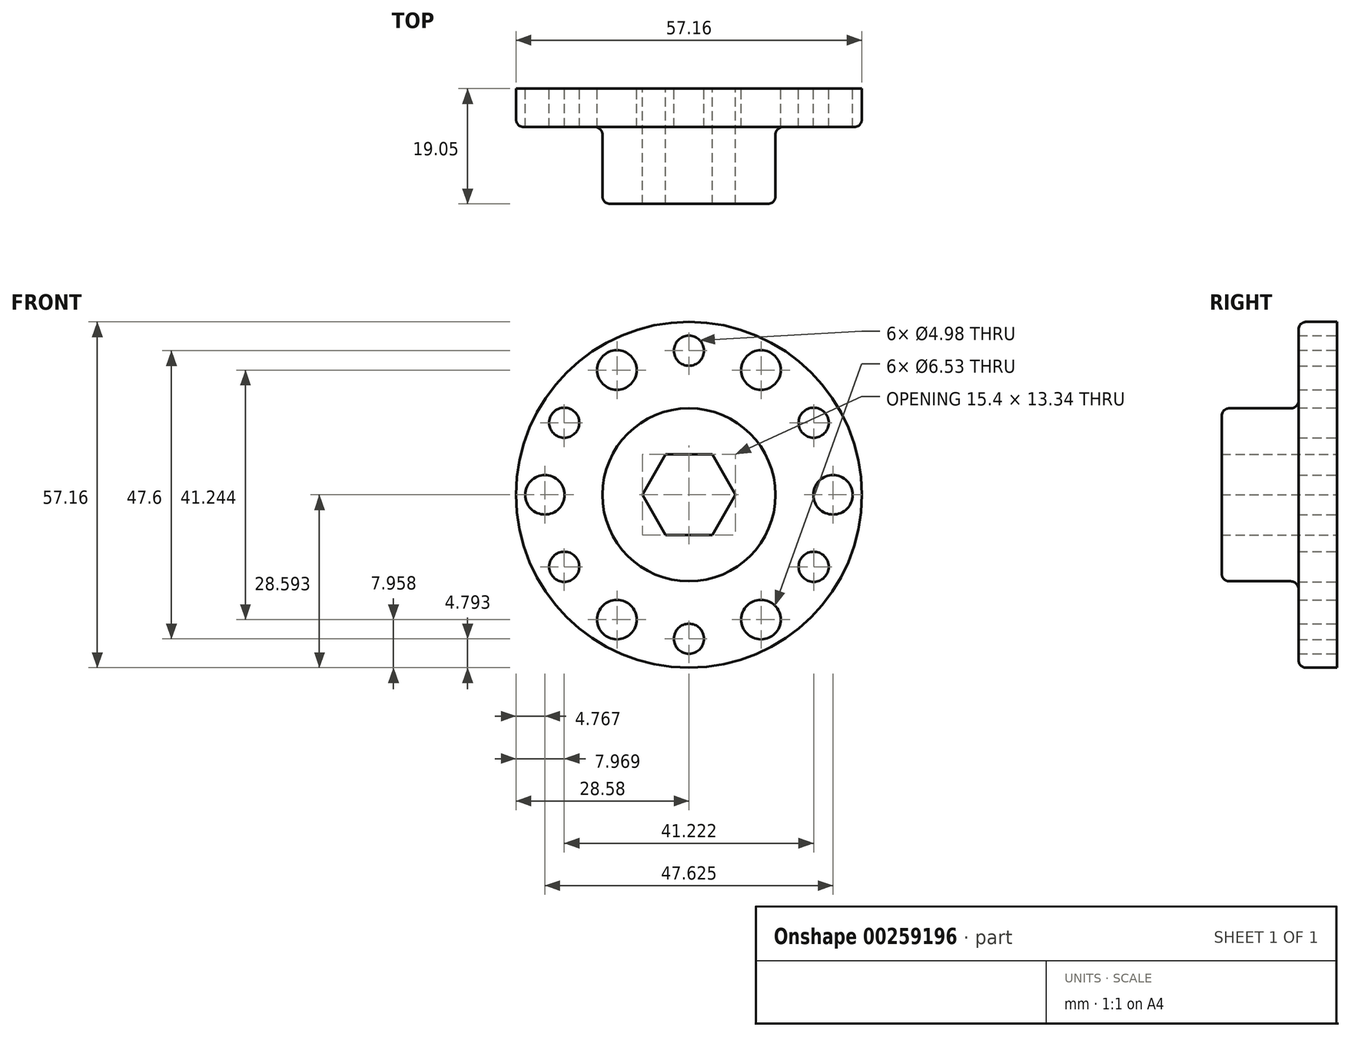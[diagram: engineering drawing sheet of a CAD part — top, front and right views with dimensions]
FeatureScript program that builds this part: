
annotation { "Feature Type Name" : "Feature", "Feature Type Description" : "" }
export const myFeature = defineFeature(function(context is Context, id is Id, definition is map)
    precondition{}
    {
        {
            var Q0;
            Q0=qCreatedBy(makeId("Front.planeOp"),FACE);
            var sketch = newSketch(context, id + "F0", { "sketchPlane" : qUnion([Q0])});
            skCircle(sketch, "E0", {"center": v(0, 0) * mm, "radius": 28.58 * mm});
            skCircle(sketch, "E1", {"center": v(0, 23.81) * mm, "radius": 2.49 * mm});
            skCircle(sketch, "E2.1.0", {"center": v(-20.61, 11.91) * mm, "radius": 2.49 * mm});
            skCircle(sketch, "E2.2.0", {"center": v(-20.61, -11.89) * mm, "radius": 2.49 * mm});
            skCircle(sketch, "E2.3.0", {"center": v(0, -23.79) * mm, "radius": 2.49 * mm});
            skCircle(sketch, "E2.4.0", {"center": v(20.61, -11.89) * mm, "radius": 2.49 * mm});
            skCircle(sketch, "E2.5.0", {"center": v(20.61, 11.91) * mm, "radius": 2.49 * mm});
            skPoint(sketch, "E2.center", {"position": v(0, 0.01) * mm});
            skCircle(sketch, "E3", {"center": v(0, 0) * mm, "radius": 14.3 * mm});
            skCircle(sketch, "E4.1.0", {"center": v(-11.9, 20.62) * mm, "radius": 3.26 * mm});
            skCircle(sketch, "E4.3.0", {"center": v(-23.81, 0) * mm, "radius": 3.26 * mm});
            skCircle(sketch, "E4.5.0", {"center": v(-11.9, -20.62) * mm, "radius": 3.26 * mm});
            skCircle(sketch, "E4.7.0", {"center": v(11.9, -20.62) * mm, "radius": 3.26 * mm});
            skCircle(sketch, "E4.9.0", {"center": v(23.81, 0) * mm, "radius": 3.26 * mm});
            skCircle(sketch, "E4.11.0", {"center": v(11.9, 20.62) * mm, "radius": 3.26 * mm});
            skCircle(sketch, "E5.cCircle", {"center": v(0, 0.01) * mm, "radius": 6.67 * mm, "construction": true});
            skLineSegment(sketch, "E5.0", {"start": v(-3.85, 6.68) * mm, "end": v(3.85, 6.68) * mm});
            skLineSegment(sketch, "E5.1", {"start": v(3.85, 6.68) * mm, "end": v(7.7, 0.01) * mm});
            skLineSegment(sketch, "E5.2", {"start": v(7.7, 0.01) * mm, "end": v(3.85, -6.65) * mm});
            skLineSegment(sketch, "E5.3", {"start": v(3.85, -6.65) * mm, "end": v(-3.85, -6.65) * mm});
            skLineSegment(sketch, "E5.4", {"start": v(-3.85, -6.65) * mm, "end": v(-7.7, 0.01) * mm});
            skLineSegment(sketch, "E5.5", {"start": v(-7.7, 0.01) * mm, "end": v(-3.85, 6.68) * mm});
            skPoint(sketch, "E5.0.midPoint", {"position": v(0, 6.68) * mm});
            skSolve(sketch);
        }
        {
            var Q0;
            Q0 = qSketchRegion(id + "F0", true);
            var Q1;
            Q1=makeQuery(id+"F0.imprint","IMPRINT",FACE,{"disambiguationData":[TD([[makeQuery(id+"F0.imprint","IMPRINT",EDGE,{"derivedFrom":sQuery(id+"F0.wireOp",EDGE,"E3")}),1.0]])]});
            extrude(context, id + "F1", {"entities" : qUnion([Q0, Q1]), "offsetDistance" : 25.4 * mm, "depth" : 6.35 * mm});
        }
        {
            var Q0;
            Q0=makeQuery(id+"F0.imprint","IMPRINT",FACE,{"disambiguationData":[TD([[makeQuery(id+"F0.imprint","IMPRINT",EDGE,{"derivedFrom":sQuery(id+"F0.wireOp",EDGE,"E3")}),1.0]])]});
            extrude(context, id + "F2", {"entities" : qUnion([Q0]), "operationType" : NewBodyOperationType.ADD, "offsetDistance" : 25.4 * mm, "depth" : 19.05 * mm});
        }
        {
            var Q0;
            Q0=makeQuery(id+"F1.opExtrude","CAP_EDGE",EDGE,{"disambiguationData":[OSD([sQuery(id+"F0.wireOp",EDGE,"E0")])],"isStart":false});
            var Q1;
            Q1=makeQuery(id+"F2.opExtrude","CAP_EDGE",EDGE,{"disambiguationData":[OSD([sQuery(id+"F0.wireOp",EDGE,"E3")])],"isStart":false});
            var Q2;
            Q2=makeQuery(id+"F2.boolean.opBoolean","INTERSECT",EDGE,{"derivedFrom":[makeQuery(id+"F1.opExtrude","CAP_FACE",FACE,{"disambiguationData":[OSD([sQuery(id+"F0.wireOp",EDGE,"E0"),sQuery(id+"F0.wireOp",EDGE,"E1"),sQuery(id+"F0.wireOp",EDGE,"E2.1.0"),sQuery(id+"F0.wireOp",EDGE,"E2.2.0"),sQuery(id+"F0.wireOp",EDGE,"E2.3.0"),sQuery(id+"F0.wireOp",EDGE,"E2.4.0"),sQuery(id+"F0.wireOp",EDGE,"E2.5.0"),sQuery(id+"F0.wireOp",EDGE,"bd753548-25c6-4d1b-81c4-4a3fece49004.0"),sQuery(id+"F0.wireOp",EDGE,"bd753548-25c6-4d1b-81c4-4a3fece49004.1"),sQuery(id+"F0.wireOp",EDGE,"bd753548-25c6-4d1b-81c4-4a3fece49004.2"),sQuery(id+"F0.wireOp",EDGE,"bd753548-25c6-4d1b-81c4-4a3fece49004.3"),sQuery(id+"F0.wireOp",EDGE,"bd753548-25c6-4d1b-81c4-4a3fece49004.4"),sQuery(id+"F0.wireOp",EDGE,"bd753548-25c6-4d1b-81c4-4a3fece49004.5")])],"isStart":false}),makeQuery(id+"F2.opExtrude","SWEPT_FACE",FACE,{"disambiguationData":[OSD([sQuery(id+"F0.wireOp",EDGE,"E3")])]})]});
            fillet(context, id + "F3", {"entities" : qUnion([Q0, Q1, Q2]), "radius" : 1.27 * mm, "tangentPropagation" : true, "allowEdgeOverflow" : false});
        }
    });
